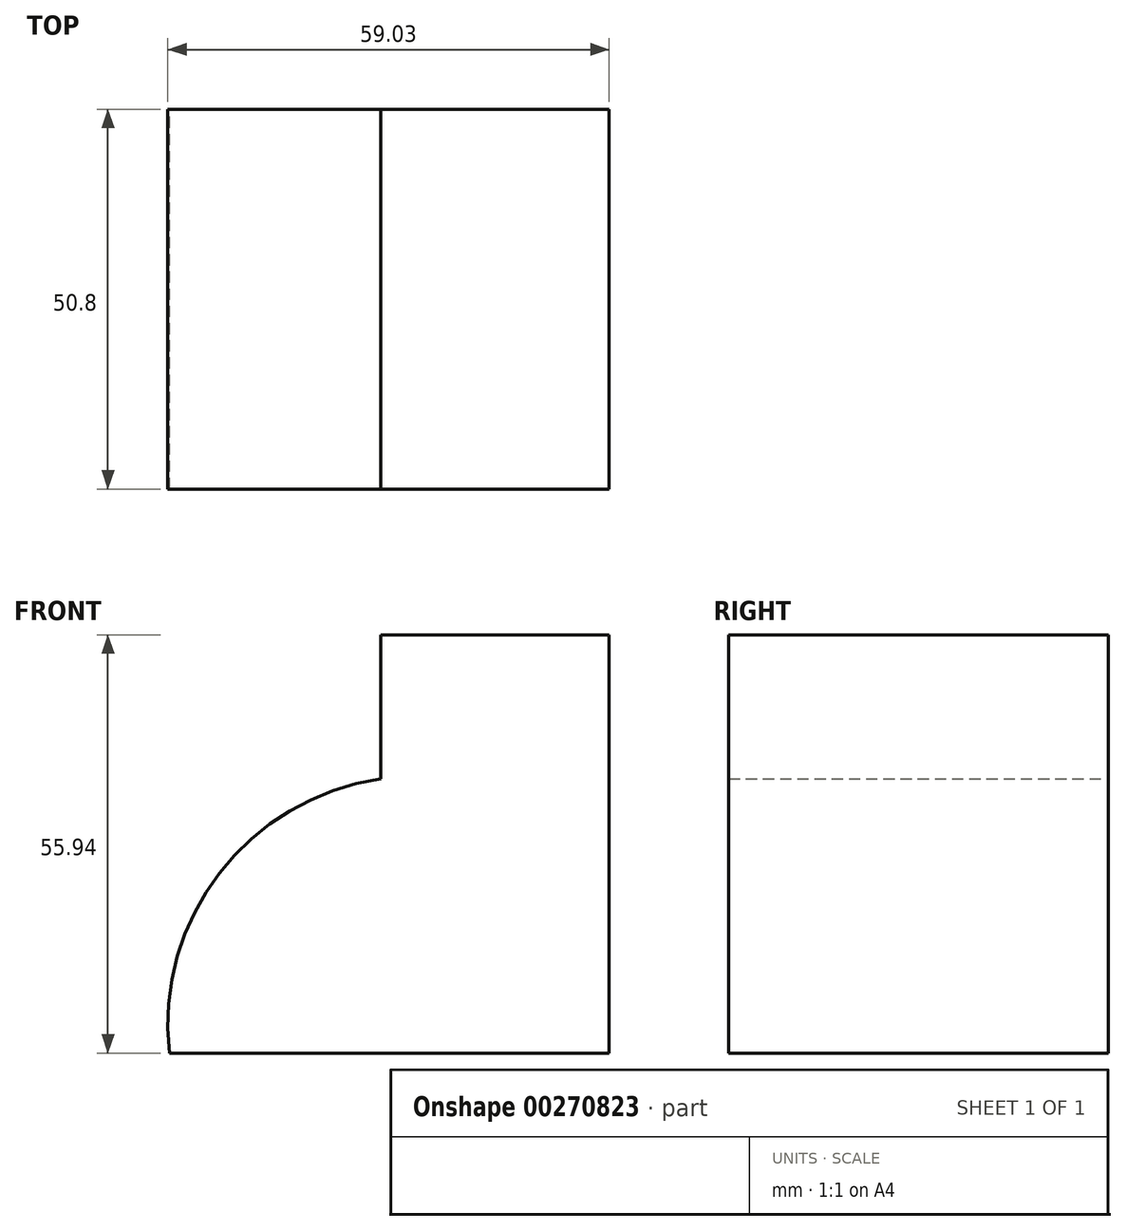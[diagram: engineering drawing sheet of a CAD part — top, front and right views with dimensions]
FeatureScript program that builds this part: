
annotation { "Feature Type Name" : "Feature", "Feature Type Description" : "" }
export const myFeature = defineFeature(function(context is Context, id is Id, definition is map)
    precondition{}
    {
        {
            var Q0;
            Q0=qCreatedBy(makeId("Front.planeOp"),FACE);
            var sketch = newSketch(context, id + "F0", { "sketchPlane" : qUnion([Q0])});
            skLineSegment(sketch, "E0", {"start": v(0, 0) * mm, "end": v(0, 55.94) * mm});
            skLineSegment(sketch, "E1", {"start": v(0, 55.94) * mm, "end": v(-30.56, 55.94) * mm});
            skLineSegment(sketch, "E2", {"start": v(-30.56, 55.94) * mm, "end": v(-30.56, 36.65) * mm});
            skLineSegment(sketch, "E3", {"start": v(0, 0) * mm, "end": v(-58.81, 0) * mm});
            skArc(sketch, "E4", {"start": v(-30.56, 36.65) * mm, "mid": v(-52.13, 24.06) * mm, "end": v(-58.81, 0) * mm});
            skSolve(sketch);
        }
        {
            var Q0;
            Q0 = qSketchRegion(id + "F0", true);
            extrude(context, id + "F1", {"entities" : qUnion([Q0]), "depth" : 50.8 * mm});
        }
    });
